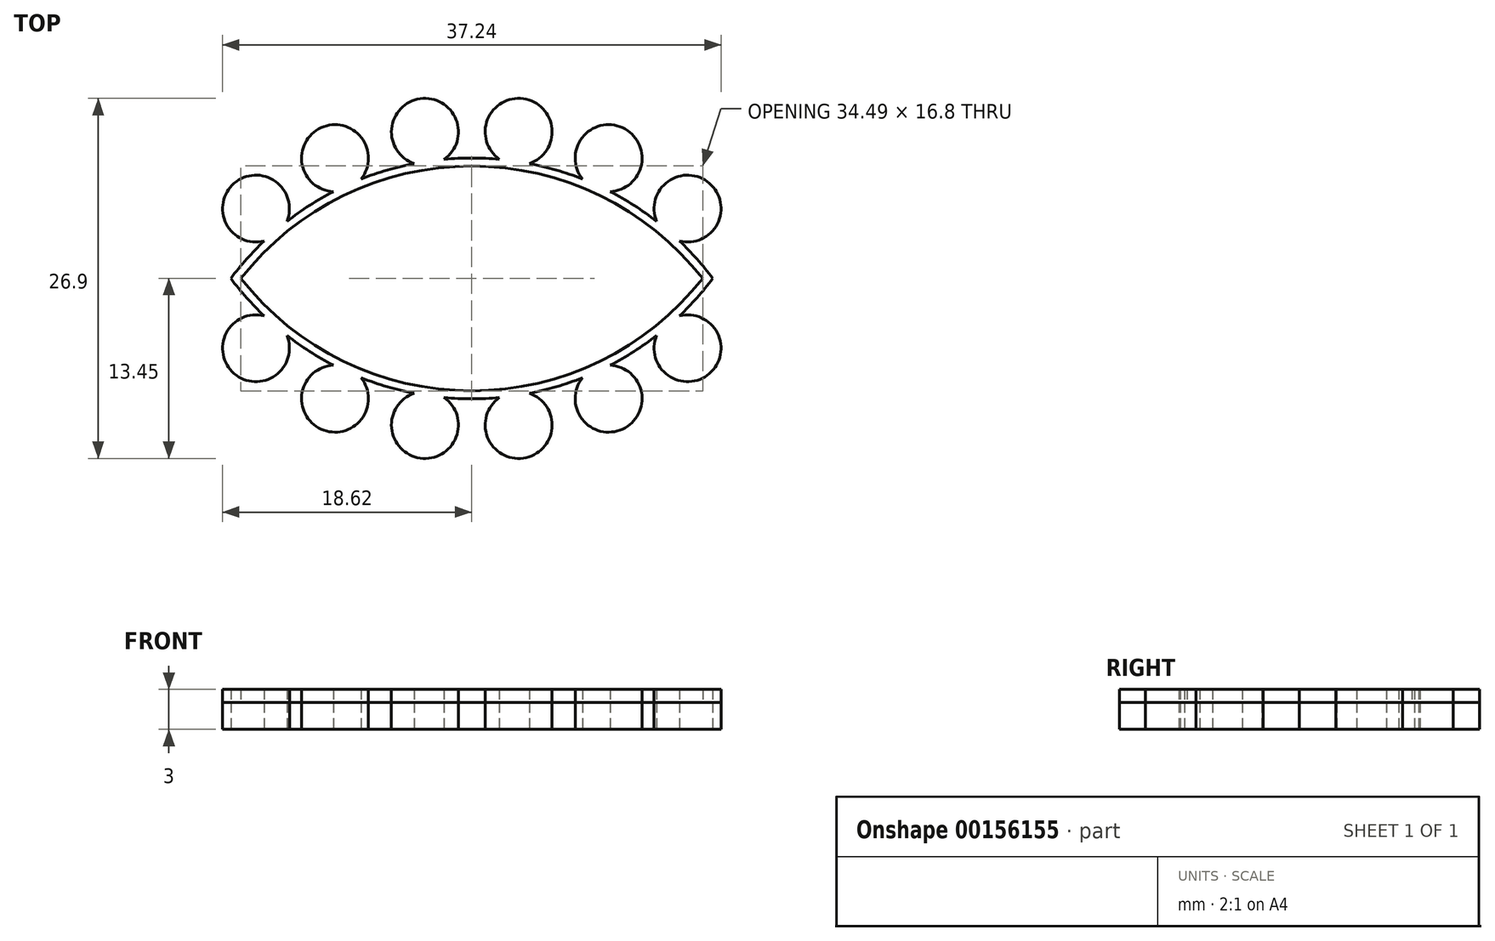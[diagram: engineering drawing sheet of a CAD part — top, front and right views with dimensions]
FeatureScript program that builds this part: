
annotation { "Feature Type Name" : "Feature", "Feature Type Description" : "" }
export const myFeature = defineFeature(function(context is Context, id is Id, definition is map)
    precondition{}
    {
        {
            var Q0;
            Q0=qCreatedBy(makeId("Top.planeOp"),FACE);
            var sketch = newSketch(context, id + "F0", { "sketchPlane" : qUnion([Q0])});
            skLineSegment(sketch, "E0", {"start": v(-7.62, 9) * mm, "end": v(8.9, 9) * mm, "construction": true});
            skLineSegment(sketch, "E1", {"start": v(18, 7.05) * mm, "end": v(18, -4.16) * mm, "construction": true});
            skLineSegment(sketch, "E2", {"start": v(-18, 11.56) * mm, "end": v(-18, -4.19) * mm, "construction": true});
            skArc(sketch, "E3", {"start": v(18, 0) * mm, "mid": v(0, 9) * mm, "end": v(-18, 0) * mm});
            skArc(sketch, "E4.0", {"start": v(17.24, 0) * mm, "mid": v(0, 8.4) * mm, "end": v(-17.24, 0) * mm});
            skCircle(sketch, "E5", {"center": v(3.5, 10.95) * mm, "radius": 2.5 * mm});
            skCircle(sketch, "E6", {"center": v(10.22, 8.99) * mm, "radius": 2.5 * mm});
            skCircle(sketch, "E7", {"center": v(16.12, 5.22) * mm, "radius": 2.5 * mm});
            skArc(sketch, "E8.0", {"start": v(17.76, -0.18) * mm, "mid": v(0, 8.7) * mm, "end": v(-17.76, -0.18) * mm, "construction": true});
            skCircle(sketch, "E9.MirrorC", {"center": v(-16.12, 5.22) * mm, "radius": 2.5 * mm});
            skCircle(sketch, "E10.MirrorC", {"center": v(-10.22, 8.99) * mm, "radius": 2.5 * mm});
            skCircle(sketch, "E11.MirrorC", {"center": v(-3.5, 10.95) * mm, "radius": 2.5 * mm});
            skArc(sketch, "E12.MirrorCS", {"start": v(-17.76, -0.18) * mm, "mid": v(0, 8.7) * mm, "end": v(17.76, -0.18) * mm, "construction": true});
            skCircle(sketch, "E13.MirrorC", {"center": v(16.12, -5.22) * mm, "radius": 2.5 * mm});
            skCircle(sketch, "E14.MirrorC", {"center": v(10.22, -8.99) * mm, "radius": 2.5 * mm});
            skCircle(sketch, "E15.MirrorC", {"center": v(-10.22, -8.99) * mm, "radius": 2.5 * mm});
            skArc(sketch, "E16.MirrorCS", {"start": v(17.24, 0) * mm, "mid": v(0, -8.4) * mm, "end": v(-17.24, 0) * mm});
            skCircle(sketch, "E17.MirrorC", {"center": v(3.5, -10.95) * mm, "radius": 2.5 * mm});
            skArc(sketch, "E18.MirrorCS", {"start": v(18, 0) * mm, "mid": v(0, -9) * mm, "end": v(-18, 0) * mm});
            skArc(sketch, "E19.MirrorCS", {"start": v(-17.76, 0.18) * mm, "mid": v(0, -8.7) * mm, "end": v(17.76, 0.18) * mm, "construction": true});
            skLineSegment(sketch, "E20.MirrorCS", {"start": v(-7.62, -9) * mm, "end": v(8.9, -9) * mm, "construction": true});
            skCircle(sketch, "E21.MirrorC", {"center": v(-16.12, -5.22) * mm, "radius": 2.5 * mm});
            skCircle(sketch, "E22.MirrorC", {"center": v(-3.5, -10.95) * mm, "radius": 2.5 * mm});
            skArc(sketch, "E23.MirrorCS", {"start": v(17.76, 0.18) * mm, "mid": v(0, -8.7) * mm, "end": v(-17.76, 0.18) * mm, "construction": true});
            skSolve(sketch);
        }
        {
            var Q0;
            Q0 = qSketchRegion(id + "F0", true);
            extrude(context, id + "F1", {"entities" : qUnion([Q0]), "depth" : 1 * mm});
        }
        {
            var Q0;
            Q0 = qSketchRegion(id + "F0", true);
            var Q1;
            Q1=makeQuery(id+"F0.imprint","IMPRINT",FACE,{"disambiguationData":[TD([[makeQuery(id+"F0.imprint","IMPRINT",EDGE,{"derivedFrom":sQuery(id+"F0.wireOp",EDGE,"E4.0")}),1.0]])]});
            extrude(context, id + "F2", {"entities" : qUnion([Q0, Q1]), "depth" : 2 * mm});
        }
        {
            var Q0;
            Q0=makeQuery(id+"F1.opExtrude","SWEPT_BODY",BODY,{"disambiguationData":[OSD([sQuery(id+"F0.wireOp",EDGE,"E3"),sQuery(id+"F0.wireOp",EDGE,"E4.0"),sQuery(id+"F0.wireOp",EDGE,"E5"),sQuery(id+"F0.wireOp",EDGE,"E6"),sQuery(id+"F0.wireOp",EDGE,"E7"),sQuery(id+"F0.wireOp",EDGE,"E9.MirrorC"),sQuery(id+"F0.wireOp",EDGE,"E10.MirrorC"),sQuery(id+"F0.wireOp",EDGE,"E11.MirrorC"),sQuery(id+"F0.wireOp",EDGE,"E13.MirrorC"),sQuery(id+"F0.wireOp",EDGE,"E14.MirrorC"),sQuery(id+"F0.wireOp",EDGE,"E15.MirrorC"),sQuery(id+"F0.wireOp",EDGE,"E16.MirrorCS"),sQuery(id+"F0.wireOp",EDGE,"E17.MirrorC"),sQuery(id+"F0.wireOp",EDGE,"E18.MirrorCS"),sQuery(id+"F0.wireOp",EDGE,"E21.MirrorC"),sQuery(id+"F0.wireOp",EDGE,"E22.MirrorC")])]});
            transform(context, id + "F3", {"entities" : qUnion([Q0]), "transformType" : TransformType.TRANSLATION_3D, "dx" : 0 * mm, "dy" : 0 * mm, "dz" : 2 * mm, "makeCopy" : false});
        }
    });
